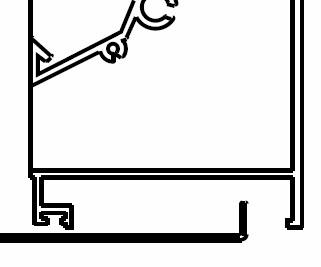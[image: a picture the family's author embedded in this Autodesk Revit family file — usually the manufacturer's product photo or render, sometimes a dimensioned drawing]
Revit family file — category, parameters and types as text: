
# Revit family: Louver_Carnes-Alum-J_Blade-Stationary-FLDC
name_source: partatom
category: Duct Accessories
revit_build: Autodesk Revit MEP 2012 (Build: 20110309_2315(x64)
units: mm (PartAtom-declared; Revit-internal decimal feet)

## types (1)
- Louver_Carnes-Alum-J_Blade-Stationary-FLDC
    04 CSI = 08 91 00
    95 CSI = 10200
    Actual Height = 24"
    Actual Width = 24"
    Assembly Code = B2010300
    Blade Material = Metal - Carnes - Steel - Galvanized
    Blade Width = 22 39/128"
    Catalog URL = http://www.carnes.com
    Default Elevation = 0"
    Depth = 4 41/256"
    Description = Extruded Aluminum Stationary J Blade Louver
    Duct Connector 1 = Duct Connection 1
    Duct Connector 2 = Duct Connection 2
    Frame Material = Metal - Carnes - Steel - Galvanized
    Height = 24"
    Manufacturer = CARNES COMPANY
    Manufacturer Fax = 608-845-6470
    Maximum Horinzontal Size = 120"W x 84"H
    Maximum System Pressure = 1.00 in-wg
    Maximum System Velocity = 812 FPM
    Maximum Vertical Size = 84"W x 120"H
    Minimum Size = 12"W x 12"H
    Model = FLDC
    Offset = 3"
    Product Line = Extruded Aluminum Stationary J Blade Louver
    Product Page URL = http://www.carnes.com
    Spec Sheet URL = http://www.carnes.com
    Subcategory = Louvers and Dampers
    URL = http://www.carnes.com
    Warranty URL = http://www.carnes.com
    Width = 24"
    ecoScorecard Product Page = http://ecoscorecard.com

## geometry (parser evidence)
native form markers: Sweep x7
no freeform markers — native parametric forms only
